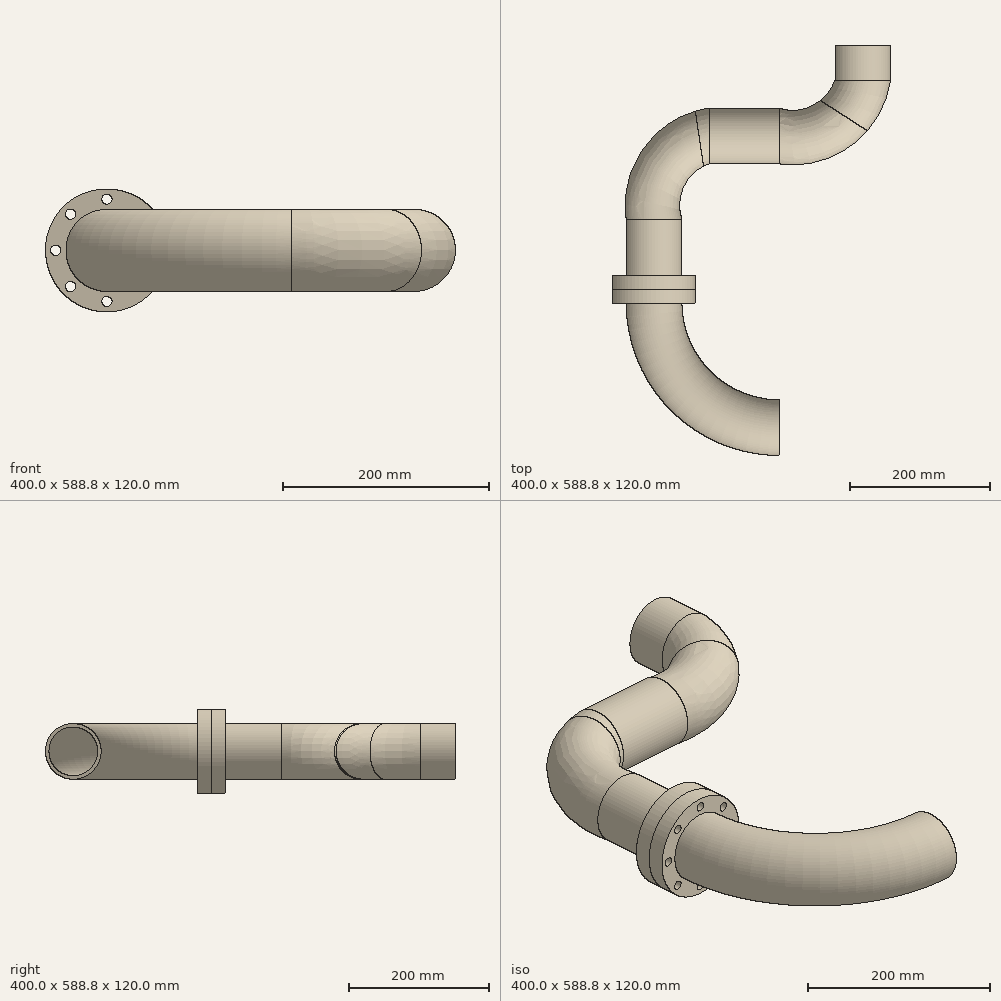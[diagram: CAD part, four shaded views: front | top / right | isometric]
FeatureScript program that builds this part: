
annotation { "Feature Type Name" : "Feature", "Feature Type Description" : "" }
export const myFeature = defineFeature(function(context is Context, id is Id, definition is map)
    precondition{}
    {
        {
            var Q0;
            Q0=qCreatedBy(makeId("Front.planeOp"),FACE);
            var sketch = newSketch(context, id + "F0", { "sketchPlane" : qUnion([Q0])});
            skCircle(sketch, "E0", {"center": v(0, 0) * mm, "radius": 60 * mm});
            skCircle(sketch, "E1", {"center": v(0, 50) * mm, "radius": 5 * mm});
            skCircle(sketch, "E2.1.0", {"center": v(-35.36, 35.36) * mm, "radius": 5 * mm});
            skCircle(sketch, "E2.2.0", {"center": v(-50, 0) * mm, "radius": 5 * mm});
            skCircle(sketch, "E2.3.0", {"center": v(-35.36, -35.36) * mm, "radius": 5 * mm});
            skCircle(sketch, "E2.4.0", {"center": v(0, -50) * mm, "radius": 5 * mm});
            skCircle(sketch, "E2.5.0", {"center": v(35.36, -35.36) * mm, "radius": 5 * mm});
            skCircle(sketch, "E2.6.0", {"center": v(50, 0) * mm, "radius": 5 * mm});
            skCircle(sketch, "E2.7.0", {"center": v(35.36, 35.36) * mm, "radius": 5 * mm});
            skCircle(sketch, "E3", {"center": v(0, 0) * mm, "radius": 35 * mm});
            skSolve(sketch);
        }
        {
            var Q0;
            Q0 = qSketchRegion(id + "F0", true);
            extrude(context, id + "F1", {"entities" : qUnion([Q0]), "depth" : 20 * mm, "offsetDistance" : 25 * mm});
        }
        {
            var Q0;
            Q0=makeQuery(id+"F1.opExtrude","CAP_FACE",FACE,{"disambiguationData":[OSD([sQuery(id+"F0.wireOp",EDGE,"E0"),sQuery(id+"F0.wireOp",EDGE,"E1"),sQuery(id+"F0.wireOp",EDGE,"E2.1.0"),sQuery(id+"F0.wireOp",EDGE,"E2.2.0"),sQuery(id+"F0.wireOp",EDGE,"E2.3.0"),sQuery(id+"F0.wireOp",EDGE,"E2.4.0"),sQuery(id+"F0.wireOp",EDGE,"E2.5.0"),sQuery(id+"F0.wireOp",EDGE,"E2.6.0"),sQuery(id+"F0.wireOp",EDGE,"E2.7.0")])],"isStart":false});
            var sketch = newSketch(context, id + "F2", { "sketchPlane" : qUnion([Q0])});
            skCircle(sketch, "E4", {"center": v(0, 0) * mm, "radius": 35 * mm});
            skCircle(sketch, "E5", {"center": v(0, 0) * mm, "radius": 40 * mm});
            skSolve(sketch);
        }
        {
            var Q0;
            Q0=qCreatedBy(makeId("Top.planeOp"),FACE);
            var sketch = newSketch(context, id + "F3", { "sketchPlane" : qUnion([Q0])});
            skLineSegment(sketch, "E6", {"start": v(0, 0) * mm, "end": v(0, 100) * mm});
            skLineSegment(sketch, "E7", {"start": v(100, 200) * mm, "end": v(200, 200) * mm});
            skLineSegment(sketch, "E8", {"start": v(300, 300) * mm, "end": v(300, 350) * mm});
            skPoint(sketch, "E9.visualSharp", {"position": v(0, 200) * mm});
            skArc(sketch, "E9.filletArc", {"start": v(85.05, 198.88) * mm, "mid": v(24.19, 165.21) * mm, "end": v(0, 100) * mm});
            skPoint(sketch, "E10.visualSharp", {"position": v(300, 200) * mm});
            skArc(sketch, "E10.filletArc", {"start": v(200, 200) * mm, "mid": v(247.85, 212.2) * mm, "end": v(284.04, 245.8) * mm});
            skPoint(sketch, "E11.visualSharp", {"position": v(100, 200) * mm});
            skArc(sketch, "E11.filletArc", {"start": v(100, 200) * mm, "mid": v(92.5, 199.72) * mm, "end": v(85.05, 198.88) * mm});
            skPoint(sketch, "E12.visualSharp", {"position": v(300, 300) * mm});
            skArc(sketch, "E12.filletArc", {"start": v(284.04, 245.8) * mm, "mid": v(295.93, 271.75) * mm, "end": v(300, 300) * mm});
            skSolve(sketch);
        }
        {
            var Q0;
            Q0=makeQuery(id+"F2.imprint","IMPRINT",FACE,{"disambiguationData":[TD([[makeQuery(id+"F2.imprint","IMPRINT",EDGE,{"derivedFrom":sQuery(id+"F2.wireOp",EDGE,"E4")}),-1.0]])]});
            var Q1;
            Q1=sQuery(id+"F3.wireOp",EDGE,"E9.filletArc");
            var Q2;
            Q2=sQuery(id+"F3.wireOp",EDGE,"E6");
            var Q3;
            Q3=sQuery(id+"F3.wireOp",EDGE,"E11.filletArc");
            var Q4;
            Q4=sQuery(id+"F3.wireOp",EDGE,"E7");
            var Q5;
            Q5=sQuery(id+"F3.wireOp",EDGE,"E10.filletArc");
            var Q6;
            Q6=sQuery(id+"F3.wireOp",EDGE,"E12.filletArc");
            var Q7;
            Q7=sQuery(id+"F3.wireOp",EDGE,"E8");
            sweep(context, id + "F4", {"profiles" : qUnion([Q0]), "path" : qUnion([Q1, Q2, Q3, Q4, Q5, Q6, Q7])});
        }
        {
            var Q0;
            Q0=makeQuery(id+"F1.opExtrude","CAP_FACE",FACE,{"disambiguationData":[OSD([sQuery(id+"F0.wireOp",EDGE,"E0"),sQuery(id+"F0.wireOp",EDGE,"E1"),sQuery(id+"F0.wireOp",EDGE,"E2.1.0"),sQuery(id+"F0.wireOp",EDGE,"E2.2.0"),sQuery(id+"F0.wireOp",EDGE,"E2.3.0"),sQuery(id+"F0.wireOp",EDGE,"E2.4.0"),sQuery(id+"F0.wireOp",EDGE,"E2.5.0"),sQuery(id+"F0.wireOp",EDGE,"E2.6.0"),sQuery(id+"F0.wireOp",EDGE,"E2.7.0"),sQuery(id+"F0.wireOp",EDGE,"E3")])],"isStart":false});
            extrude(context, id + "F5", {"entities" : qUnion([Q0]), "depth" : 20 * mm, "offsetDistance" : 25 * mm});
        }
        {
            var Q0;
            Q0=makeQuery(id+"F5.opExtrude","CAP_FACE",FACE,{"disambiguationData":[OSD([sQuery(id+"F0.wireOp",EDGE,"E0"),sQuery(id+"F0.wireOp",EDGE,"E1"),sQuery(id+"F0.wireOp",EDGE,"E2.1.0"),sQuery(id+"F0.wireOp",EDGE,"E2.2.0"),sQuery(id+"F0.wireOp",EDGE,"E2.3.0"),sQuery(id+"F0.wireOp",EDGE,"E2.4.0"),sQuery(id+"F0.wireOp",EDGE,"E2.5.0"),sQuery(id+"F0.wireOp",EDGE,"E2.6.0"),sQuery(id+"F0.wireOp",EDGE,"E2.7.0"),sQuery(id+"F0.wireOp",EDGE,"E3")])],"isStart":false});
            var sketch = newSketch(context, id + "F6", { "sketchPlane" : qUnion([Q0])});
            skCircle(sketch, "E13", {"center": v(0, 0) * mm, "radius": 35 * mm});
            skCircle(sketch, "E14", {"center": v(0, 0) * mm, "radius": 40 * mm});
            skSolve(sketch);
        }
        {
            var Q0;
            Q0=qCreatedBy(makeId("Top.planeOp"),FACE);
            var sketch = newSketch(context, id + "F7", { "sketchPlane" : qUnion([Q0])});
            skLineSegment(sketch, "E15", {"start": v(0, -38.75) * mm, "end": v(180, -38.75) * mm, "construction": true});
            skLineSegment(sketch, "E16", {"start": v(180, -38.75) * mm, "end": v(180, -218.75) * mm, "construction": true});
            skArc(sketch, "E17", {"start": v(0, -38.75) * mm, "mid": v(52.72, -166.03) * mm, "end": v(180, -218.75) * mm});
            skSolve(sketch);
        }
        {
            var Q0;
            Q0=makeQuery(id+"F6.imprint","IMPRINT",FACE,{"disambiguationData":[TD([[makeQuery(id+"F6.imprint","IMPRINT",EDGE,{"derivedFrom":sQuery(id+"F6.wireOp",EDGE,"E13")}),-1.0]])]});
            var Q1;
            Q1=sQuery(id+"F7.wireOp",EDGE,"E17");
            sweep(context, id + "F8", {"operationType" : NewBodyOperationType.ADD, "profiles" : qUnion([Q0]), "path" : qUnion([Q1])});
        }
    });
